# Revit family: LUXI_HIGH BAY LIGHT_PA
name_source: partatom
category: Apparecchi per illuminazione
revit_build: Autodesk Revit 2016 (Build: 20161004_0715(x64)
units: mm (PartAtom-declared; Revit-internal decimal feet)

## family parameters
Condiviso = No
Host = Superficie
Numero OmniClass = 23.80.70.00
Punto di calcolo locali = Sì
Quota connettore circolare = Usa diametro
Sorgente d'illuminazione = Sì
Taglio con vuoti quando caricato = No
Tipo di parte = Normale
Titolo OmniClass = Lighting

## types (2) — shared parameters
Angolo inclinazione = -90.00°
CRI = ≥80 (typ.)
Carico apparente = 120 VA
Certifications = CE / RohS
Code = HBPA150085W840D
Color = White
Descrizione = LED Projector
Diameter = 350 mm  [stored 1.14829 ft]
Dimming = 1-10V
Dust and water protection rating = IP 65 (front)
Emetti da diametro cerchio = 190 mm
Energy class = A+
File diagramma fotometrico = HBPA150085W840D Luxi SERIE PA 150W 4000K 120W.IES
Filtro dei colori = 16777215
H = 273 mm  [stored 0.895669 ft]
IFCExportAs = IfcLightFixtureType
Impact rating = IK10 (20 Joule)
Installation = Suspended
Lifetime = L70B20 50.000h
Light distribution = 90% downlight / 10% luce edge light
Light source = LED SMD
Masterformat 2016 code = 26.50.00
Masterformat 2016 description = Lighting
Material 1 = Aluminum_White
Material 3 = Polycarbonate_Transparent
Modello = PA Series| High Bay Light
Operating temperature = -40°C / +45°C
Optics = Beam 85°
Photobiological risk group = RG0
Power factor = ≥0,95 (typ.)
Power supply = Included
Produttore = Luxi Illuminazione S.r.l.
Prospetto di default = 2000 mm
Protection class = I
Rated supply voltage = 220-240V AC / 50-60 Hz
Rendi la forma visibile nel rendering = No
Review = 3
Size = Ø350x273
Step MacAdam (SDCM) = <4
URL = https://www.luxi.lighting
Uniclass 2015 code = EF_70_80
Uniclass 2015 description = Lighting
Variazione temperatura colore lampada con luminosità attenuata = <Nessuno>
Warranty = 7 years
Wattage = 120 W
Weight = 6.70 kg

## per-type parameters (varying)
| type | Material 2 |
| HBPA150085W840D | Polycarbonate_Transparent |
| HBPA150085W840D_120W | Polycarbonate |

note: [stored X ft] marks values corroborated as IEEE doubles in the binary element streams (Revit-internal decimal feet)

## geometry (parser evidence)
native form markers: Blend x2
no freeform markers — native parametric forms only
